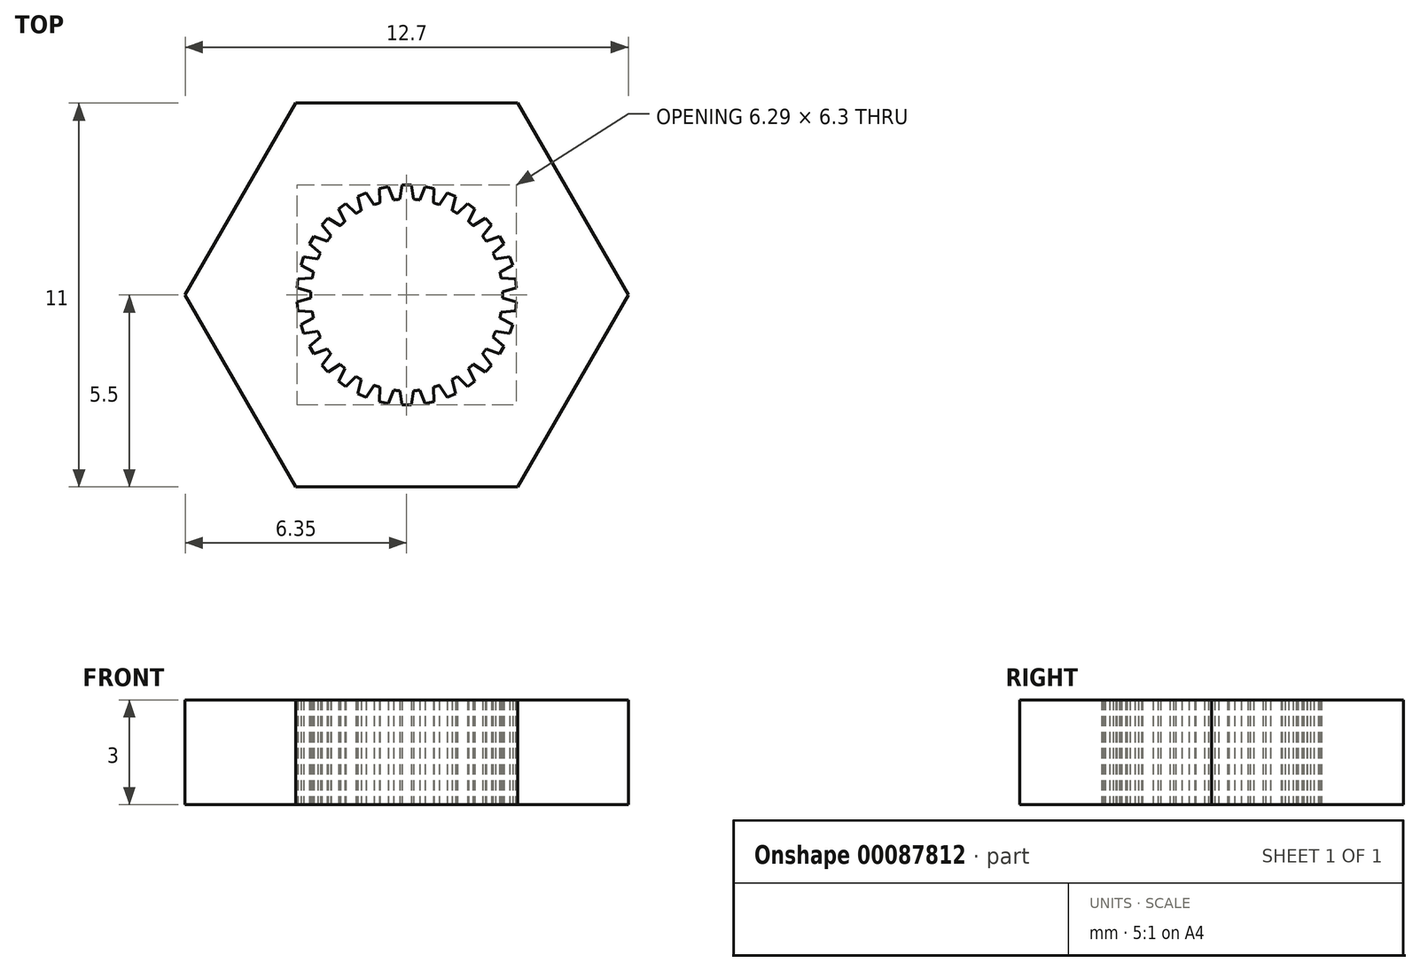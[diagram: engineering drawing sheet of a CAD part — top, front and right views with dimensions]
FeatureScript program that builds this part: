
annotation { "Feature Type Name" : "Feature", "Feature Type Description" : "" }
export const myFeature = defineFeature(function(context is Context, id is Id, definition is map)
    precondition{}
    {
        {
            var Q0;
            Q0=qCreatedBy(makeId("Top.planeOp"),FACE);
            var sketch = newSketch(context, id + "F0", { "sketchPlane" : qUnion([Q0])});
            skCircle(sketch, "E0.cCircle", {"center": v(0, 0) * mm, "radius": 5.5 * mm, "construction": true});
            skLineSegment(sketch, "E0.0", {"start": v(-3.18, 5.5) * mm, "end": v(3.18, 5.5) * mm});
            skLineSegment(sketch, "E0.1", {"start": v(3.18, 5.5) * mm, "end": v(6.35, 0) * mm});
            skLineSegment(sketch, "E0.2", {"start": v(6.35, 0) * mm, "end": v(3.18, -5.5) * mm});
            skLineSegment(sketch, "E0.3", {"start": v(3.18, -5.5) * mm, "end": v(-3.18, -5.5) * mm});
            skLineSegment(sketch, "E0.4", {"start": v(-3.18, -5.5) * mm, "end": v(-6.35, 0) * mm});
            skLineSegment(sketch, "E0.5", {"start": v(-6.35, 0) * mm, "end": v(-3.18, 5.5) * mm});
            skPoint(sketch, "E0.0.midPoint", {"position": v(0, 5.5) * mm});
            skCircle(sketch, "E1", {"center": v(0, 0) * mm, "radius": 2.75 * mm});
            skLineSegment(sketch, "E2", {"start": v(0, 0) * mm, "end": v(0, 2.75) * mm, "construction": true});
            skLineSegment(sketch, "E3", {"start": v(-0.2, 2.74) * mm, "end": v(-0.13, 3.15) * mm});
            skLineSegment(sketch, "E4", {"start": v(-0.13, 3.15) * mm, "end": v(0.13, 3.15) * mm});
            skLineSegment(sketch, "E5", {"start": v(0.13, 3.15) * mm, "end": v(0.2, 2.74) * mm});
            skLineSegment(sketch, "E6.1.0", {"start": v(-0.53, 3.1) * mm, "end": v(-0.37, 2.72) * mm});
            skLineSegment(sketch, "E6.1.1", {"start": v(-0.78, 3.05) * mm, "end": v(-0.53, 3.1) * mm});
            skLineSegment(sketch, "E6.1.2", {"start": v(-0.77, 2.64) * mm, "end": v(-0.78, 3.05) * mm});
            skLineSegment(sketch, "E6.2.0", {"start": v(-1.16, 2.93) * mm, "end": v(-0.93, 2.59) * mm});
            skLineSegment(sketch, "E6.2.1", {"start": v(-1.4, 2.83) * mm, "end": v(-1.16, 2.93) * mm});
            skLineSegment(sketch, "E6.2.2", {"start": v(-1.3, 2.42) * mm, "end": v(-1.4, 2.83) * mm});
            skLineSegment(sketch, "E6.3.0", {"start": v(-1.75, 2.62) * mm, "end": v(-1.45, 2.34) * mm});
            skLineSegment(sketch, "E6.3.1", {"start": v(-1.96, 2.47) * mm, "end": v(-1.75, 2.62) * mm});
            skLineSegment(sketch, "E6.3.2", {"start": v(-1.77, 2.1) * mm, "end": v(-1.96, 2.47) * mm});
            skLineSegment(sketch, "E6.4.0", {"start": v(-2.26, 2.2) * mm, "end": v(-1.9, 1.98) * mm});
            skLineSegment(sketch, "E6.4.1", {"start": v(-2.43, 2.01) * mm, "end": v(-2.26, 2.2) * mm});
            skLineSegment(sketch, "E6.4.2", {"start": v(-2.17, 1.69) * mm, "end": v(-2.43, 2.01) * mm});
            skLineSegment(sketch, "E6.5.0", {"start": v(-2.66, 1.69) * mm, "end": v(-2.28, 1.54) * mm});
            skLineSegment(sketch, "E6.5.1", {"start": v(-2.8, 1.46) * mm, "end": v(-2.66, 1.69) * mm});
            skLineSegment(sketch, "E6.5.2", {"start": v(-2.48, 1.2) * mm, "end": v(-2.8, 1.46) * mm});
            skLineSegment(sketch, "E6.6.0", {"start": v(-2.96, 1.1) * mm, "end": v(-2.55, 1.04) * mm});
            skLineSegment(sketch, "E6.6.1", {"start": v(-3.04, 0.85) * mm, "end": v(-2.96, 1.1) * mm});
            skLineSegment(sketch, "E6.6.2", {"start": v(-2.67, 0.66) * mm, "end": v(-3.04, 0.85) * mm});
            skLineSegment(sketch, "E6.7.0", {"start": v(-3.12, 0.46) * mm, "end": v(-2.7, 0.49) * mm});
            skLineSegment(sketch, "E6.7.1", {"start": v(-3.15, 0.2) * mm, "end": v(-3.12, 0.46) * mm});
            skLineSegment(sketch, "E6.7.2", {"start": v(-2.75, 0.09) * mm, "end": v(-3.15, 0.2) * mm});
            skLineSegment(sketch, "E6.8.0", {"start": v(-3.15, -0.2) * mm, "end": v(-2.75, -0.09) * mm});
            skLineSegment(sketch, "E6.8.1", {"start": v(-3.12, -0.46) * mm, "end": v(-3.15, -0.2) * mm});
            skLineSegment(sketch, "E6.8.2", {"start": v(-2.7, -0.49) * mm, "end": v(-3.12, -0.46) * mm});
            skLineSegment(sketch, "E6.9.0", {"start": v(-3.04, -0.85) * mm, "end": v(-2.67, -0.66) * mm});
            skLineSegment(sketch, "E6.9.1", {"start": v(-2.96, -1.1) * mm, "end": v(-3.04, -0.85) * mm});
            skLineSegment(sketch, "E6.9.2", {"start": v(-2.55, -1.04) * mm, "end": v(-2.96, -1.1) * mm});
            skLineSegment(sketch, "E6.10.0", {"start": v(-2.8, -1.46) * mm, "end": v(-2.48, -1.2) * mm});
            skLineSegment(sketch, "E6.10.1", {"start": v(-2.66, -1.69) * mm, "end": v(-2.8, -1.46) * mm});
            skLineSegment(sketch, "E6.10.2", {"start": v(-2.28, -1.54) * mm, "end": v(-2.66, -1.69) * mm});
            skLineSegment(sketch, "E6.11.0", {"start": v(-2.43, -2.01) * mm, "end": v(-2.17, -1.69) * mm});
            skLineSegment(sketch, "E6.11.1", {"start": v(-2.26, -2.2) * mm, "end": v(-2.43, -2.01) * mm});
            skLineSegment(sketch, "E6.11.2", {"start": v(-1.9, -1.98) * mm, "end": v(-2.26, -2.2) * mm});
            skLineSegment(sketch, "E6.12.0", {"start": v(-1.96, -2.47) * mm, "end": v(-1.77, -2.1) * mm});
            skLineSegment(sketch, "E6.12.1", {"start": v(-1.75, -2.62) * mm, "end": v(-1.96, -2.47) * mm});
            skLineSegment(sketch, "E6.12.2", {"start": v(-1.45, -2.34) * mm, "end": v(-1.75, -2.62) * mm});
            skLineSegment(sketch, "E6.13.0", {"start": v(-1.4, -2.83) * mm, "end": v(-1.3, -2.42) * mm});
            skLineSegment(sketch, "E6.13.1", {"start": v(-1.16, -2.93) * mm, "end": v(-1.4, -2.83) * mm});
            skLineSegment(sketch, "E6.13.2", {"start": v(-0.93, -2.59) * mm, "end": v(-1.16, -2.93) * mm});
            skLineSegment(sketch, "E6.14.0", {"start": v(-0.78, -3.05) * mm, "end": v(-0.77, -2.64) * mm});
            skLineSegment(sketch, "E6.14.1", {"start": v(-0.53, -3.1) * mm, "end": v(-0.78, -3.05) * mm});
            skLineSegment(sketch, "E6.14.2", {"start": v(-0.37, -2.72) * mm, "end": v(-0.53, -3.1) * mm});
            skLineSegment(sketch, "E6.15.0", {"start": v(-0.13, -3.15) * mm, "end": v(-0.2, -2.74) * mm});
            skLineSegment(sketch, "E6.15.1", {"start": v(0.13, -3.15) * mm, "end": v(-0.13, -3.15) * mm});
            skLineSegment(sketch, "E6.15.2", {"start": v(0.2, -2.74) * mm, "end": v(0.13, -3.15) * mm});
            skLineSegment(sketch, "E6.16.0", {"start": v(0.53, -3.1) * mm, "end": v(0.37, -2.72) * mm});
            skLineSegment(sketch, "E6.16.1", {"start": v(0.78, -3.05) * mm, "end": v(0.53, -3.1) * mm});
            skLineSegment(sketch, "E6.16.2", {"start": v(0.77, -2.64) * mm, "end": v(0.78, -3.05) * mm});
            skLineSegment(sketch, "E6.17.0", {"start": v(1.16, -2.93) * mm, "end": v(0.93, -2.59) * mm});
            skLineSegment(sketch, "E6.17.1", {"start": v(1.4, -2.83) * mm, "end": v(1.16, -2.93) * mm});
            skLineSegment(sketch, "E6.17.2", {"start": v(1.3, -2.42) * mm, "end": v(1.4, -2.83) * mm});
            skLineSegment(sketch, "E6.18.0", {"start": v(1.75, -2.62) * mm, "end": v(1.45, -2.34) * mm});
            skLineSegment(sketch, "E6.18.1", {"start": v(1.96, -2.47) * mm, "end": v(1.75, -2.62) * mm});
            skLineSegment(sketch, "E6.18.2", {"start": v(1.77, -2.1) * mm, "end": v(1.96, -2.47) * mm});
            skLineSegment(sketch, "E6.19.0", {"start": v(2.26, -2.2) * mm, "end": v(1.9, -1.98) * mm});
            skLineSegment(sketch, "E6.19.1", {"start": v(2.43, -2.01) * mm, "end": v(2.26, -2.2) * mm});
            skLineSegment(sketch, "E6.19.2", {"start": v(2.17, -1.69) * mm, "end": v(2.43, -2.01) * mm});
            skLineSegment(sketch, "E6.20.0", {"start": v(2.66, -1.69) * mm, "end": v(2.28, -1.54) * mm});
            skLineSegment(sketch, "E6.20.1", {"start": v(2.8, -1.46) * mm, "end": v(2.66, -1.69) * mm});
            skLineSegment(sketch, "E6.20.2", {"start": v(2.48, -1.2) * mm, "end": v(2.8, -1.46) * mm});
            skLineSegment(sketch, "E6.21.0", {"start": v(2.96, -1.1) * mm, "end": v(2.55, -1.04) * mm});
            skLineSegment(sketch, "E6.21.1", {"start": v(3.04, -0.85) * mm, "end": v(2.96, -1.1) * mm});
            skLineSegment(sketch, "E6.21.2", {"start": v(2.67, -0.66) * mm, "end": v(3.04, -0.85) * mm});
            skLineSegment(sketch, "E6.22.0", {"start": v(3.12, -0.46) * mm, "end": v(2.7, -0.49) * mm});
            skLineSegment(sketch, "E6.22.1", {"start": v(3.15, -0.2) * mm, "end": v(3.12, -0.46) * mm});
            skLineSegment(sketch, "E6.22.2", {"start": v(2.75, -0.09) * mm, "end": v(3.15, -0.2) * mm});
            skLineSegment(sketch, "E6.23.0", {"start": v(3.15, 0.2) * mm, "end": v(2.75, 0.09) * mm});
            skLineSegment(sketch, "E6.23.1", {"start": v(3.12, 0.46) * mm, "end": v(3.15, 0.2) * mm});
            skLineSegment(sketch, "E6.23.2", {"start": v(2.7, 0.49) * mm, "end": v(3.12, 0.46) * mm});
            skLineSegment(sketch, "E6.24.0", {"start": v(3.04, 0.85) * mm, "end": v(2.67, 0.66) * mm});
            skLineSegment(sketch, "E6.24.1", {"start": v(2.96, 1.1) * mm, "end": v(3.04, 0.85) * mm});
            skLineSegment(sketch, "E6.24.2", {"start": v(2.55, 1.04) * mm, "end": v(2.96, 1.1) * mm});
            skLineSegment(sketch, "E6.25.0", {"start": v(2.8, 1.46) * mm, "end": v(2.48, 1.2) * mm});
            skLineSegment(sketch, "E6.25.1", {"start": v(2.66, 1.69) * mm, "end": v(2.8, 1.46) * mm});
            skLineSegment(sketch, "E6.25.2", {"start": v(2.28, 1.54) * mm, "end": v(2.66, 1.69) * mm});
            skLineSegment(sketch, "E6.26.0", {"start": v(2.43, 2.01) * mm, "end": v(2.17, 1.69) * mm});
            skLineSegment(sketch, "E6.26.1", {"start": v(2.26, 2.2) * mm, "end": v(2.43, 2.01) * mm});
            skLineSegment(sketch, "E6.26.2", {"start": v(1.9, 1.98) * mm, "end": v(2.26, 2.2) * mm});
            skLineSegment(sketch, "E6.27.0", {"start": v(1.96, 2.47) * mm, "end": v(1.77, 2.1) * mm});
            skLineSegment(sketch, "E6.27.1", {"start": v(1.75, 2.62) * mm, "end": v(1.96, 2.47) * mm});
            skLineSegment(sketch, "E6.27.2", {"start": v(1.45, 2.34) * mm, "end": v(1.75, 2.62) * mm});
            skLineSegment(sketch, "E6.28.0", {"start": v(1.4, 2.83) * mm, "end": v(1.3, 2.42) * mm});
            skLineSegment(sketch, "E6.28.1", {"start": v(1.16, 2.93) * mm, "end": v(1.4, 2.83) * mm});
            skLineSegment(sketch, "E6.28.2", {"start": v(0.93, 2.59) * mm, "end": v(1.16, 2.93) * mm});
            skLineSegment(sketch, "E6.29.0", {"start": v(0.78, 3.05) * mm, "end": v(0.77, 2.64) * mm});
            skLineSegment(sketch, "E6.29.1", {"start": v(0.53, 3.1) * mm, "end": v(0.78, 3.05) * mm});
            skLineSegment(sketch, "E6.29.2", {"start": v(0.37, 2.72) * mm, "end": v(0.53, 3.1) * mm});
            skSolve(sketch);
        }
        {
            var Q0;
            Q0=qSketchRegion(id+"F0",true);
            extrude(context, id + "F1", {"entities" : qUnion([Q0]), "depth" : 3 * mm});
        }
    });
